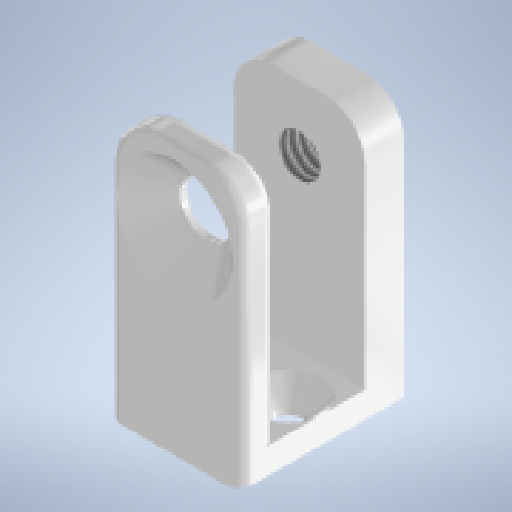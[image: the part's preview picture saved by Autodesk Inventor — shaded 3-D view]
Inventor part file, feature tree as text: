
AUTODESK INVENTOR PART (.ipt)
format: ipt  version: 2025 (Build 290162010, 162A)  size: 276,480 bytes
history: native  units: mm
features: sketch x5, hole x3, extrude x2, fillet x2
ambient origin geometry x8: Origin, YZ Plane, XZ Plane, XY Plane, X Axis, Y Axis, Z Axis, Center Point
bodies: Volumenkörper1 (feature_tree)
feature tree (12):
  extrude  "Extrusion1"  Depth=3.0mm
  fillet  "Rundung1"  Radius=3.0mm
  hole  "Bohrung1"  [1 undecoded]
  extrude  "Extrusion2"  Depth=2.0mm
  hole  "Bohrung2"  [1 undecoded]
  hole  "Bohrung3"  [1 undecoded]
  fillet  "Rundung2"  Radius=6.3mm
  sketch  "Skizze1"  dims[d0=10.0mm d1=3.0mm d2=3.0mm]
  sketch  "Skizze2"  dims[d3=6.6mm d5=20.0mm d6=0.0mm]
  sketch  "Skizze3"  dims[d7=3.0mm]
  sketch  "Skizze4"  dims[d8=3.242mm d9=8.0mm d10=9.0mm d11=14.0mm d12=90.0deg d13=11.8mm d14=20.594885mm d15=2.0mm]
  sketch  "Skizze5"  dims[d16=20.0mm d17=0.0mm d19=2.0mm d20=8.0mm d21=5.0mm d22=2.0mm d23=90.0deg d24=8.0mm d25=20.594885mm d26=4.0mm d27=8.0mm d28=4.0mm d29=2.0mm d30=90.0deg d31=5.0mm d32=20.594885mm d34=5.0mm d35=9.0mm d36=6.3mm d37=5.0mm d38=9.0mm d40=9.0mm d41=0.0mm d42=1.0mm]
note: 3 required parameter values undecoded (feature->parameter linkage not recoverable at this tier; creation-order binding heuristic only, values carry confidence <= 0.55)
